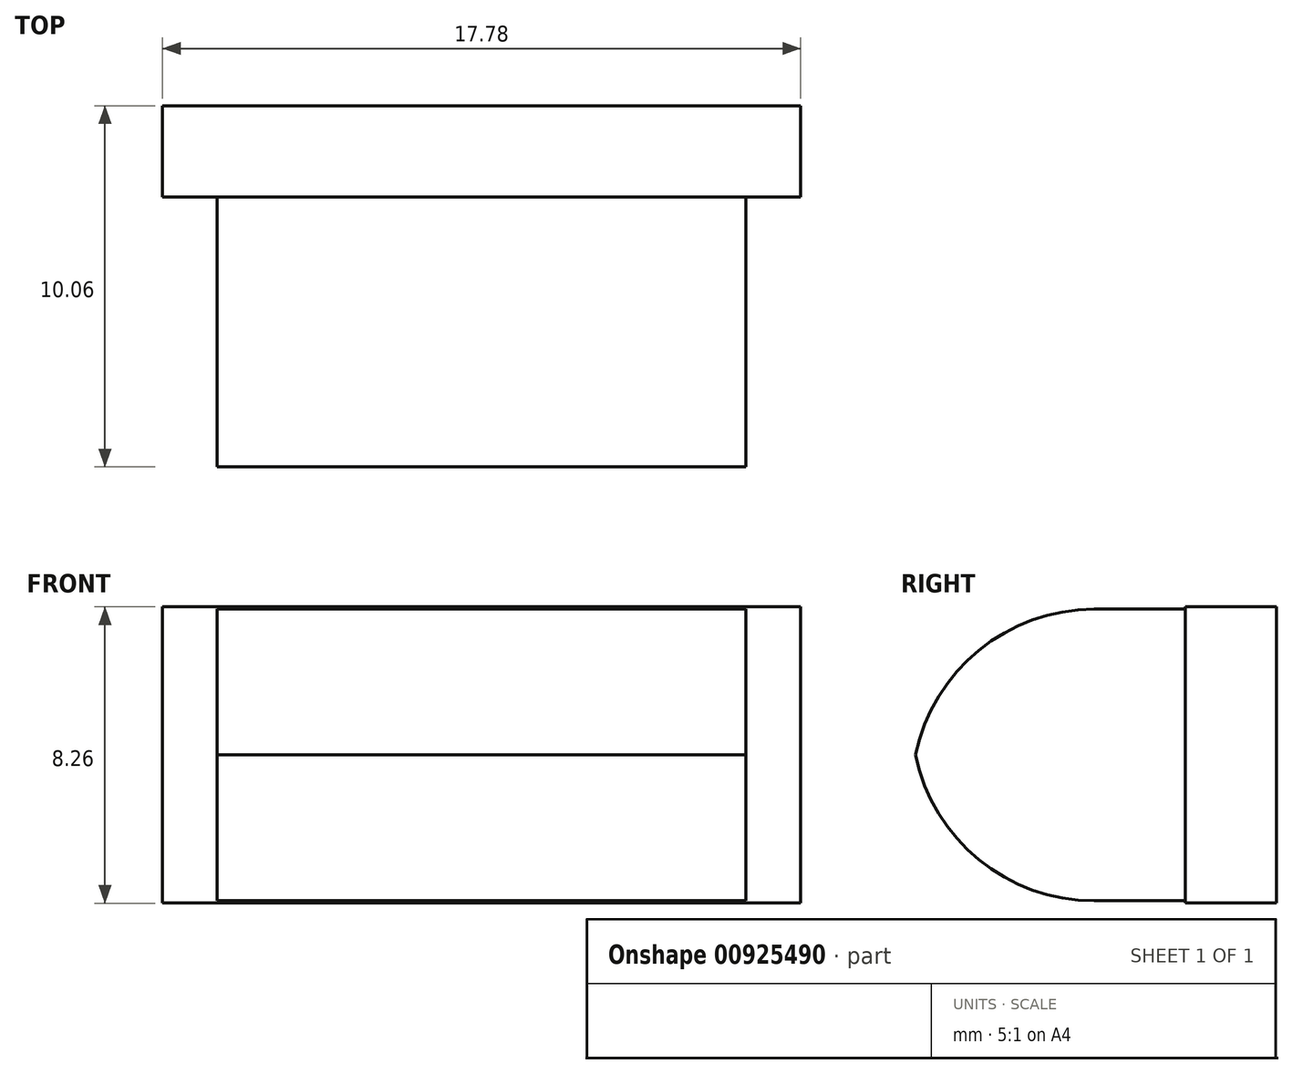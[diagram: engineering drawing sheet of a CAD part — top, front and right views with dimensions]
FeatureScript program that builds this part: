
annotation { "Feature Type Name" : "Feature", "Feature Type Description" : "" }
export const myFeature = defineFeature(function(context is Context, id is Id, definition is map)
    precondition{}
    {
        {
            var Q0;
            Q0=qCreatedBy(makeId("Front.planeOp"),FACE);
            var sketch = newSketch(context, id + "F0", { "sketchPlane" : qUnion([Q0])});
            skLineSegment(sketch, "E0.bottom", {"start": v(-8.89, -4.13) * mm, "end": v(8.9, -4.13) * mm});
            skLineSegment(sketch, "E0.top", {"start": v(-8.9, 4.13) * mm, "end": v(8.89, 4.13) * mm});
            skLineSegment(sketch, "E0.left", {"start": v(-8.89, -4.13) * mm, "end": v(-8.9, 4.13) * mm});
            skLineSegment(sketch, "E0.right", {"start": v(8.9, -4.13) * mm, "end": v(8.9, 4.13) * mm});
            skPoint(sketch, "E0.middle", {"position": v(0, 0) * mm});
            skSolve(sketch);
        }
        {
            var Q0;
            Q0 = qSketchRegion(id + "F0", true);
            extrude(context, id + "F1", {"entities" : qUnion([Q0]), "depth" : 2.54 * mm, "offsetDistance" : 25.4 * mm});
        }
        {
            var Q0;
            Q0=qCreatedBy(makeId("Front.planeOp"),FACE);
            var sketch = newSketch(context, id + "F2", { "sketchPlane" : qUnion([Q0])});
            skLineSegment(sketch, "E1.bottom", {"start": v(-7.37, -4.06) * mm, "end": v(7.37, -4.06) * mm});
            skLineSegment(sketch, "E1.top", {"start": v(-7.37, 4.06) * mm, "end": v(7.37, 4.06) * mm});
            skLineSegment(sketch, "E1.left", {"start": v(-7.37, -4.06) * mm, "end": v(-7.37, 4.06) * mm});
            skLineSegment(sketch, "E1.right", {"start": v(7.37, -4.06) * mm, "end": v(7.37, 4.06) * mm});
            skPoint(sketch, "E1.middle", {"position": v(0, 0) * mm});
            skSolve(sketch);
        }
        {
            var Q0;
            Q0 = qSketchRegion(id + "F2", true);
            extrude(context, id + "F3", {"entities" : qUnion([Q0]), "operationType" : NewBodyOperationType.ADD, "depth" : 10.16 * mm, "offsetDistance" : 25.4 * mm});
        }
        {
            var Q0;
            Q0=makeQuery(id+"F3.opExtrude","CAP_EDGE",EDGE,{"disambiguationData":[OSD([sQuery(id+"F2.wireOp",EDGE,"E1.top")])],"isStart":false});
            var Q1;
            Q1=makeQuery(id+"F3.opExtrude","CAP_EDGE",EDGE,{"disambiguationData":[OSD([sQuery(id+"F2.wireOp",EDGE,"E1.bottom")])],"isStart":false});
            fillet(context, id + "F4", {"entities" : qUnion([Q0, Q1]), "radius" : 5.08 * mm, "tangentPropagation" : true, "allowEdgeOverflow" : false});
        }
    });
